# Revit family: 06-35-013-DN50-400
name_source: partatom
category: Pipe Accessories
units: mm (PartAtom-declared; Revit-internal decimal feet)

## family parameters
Always vertical = No
Cut with Voids When Loaded = No
Part Type = Valve - Breaks Into
Round Connector Dimension = Use Diameter
Shared = No
Work Plane-Based = No

## types (12) — shared parameters
Body_Wallthickness = 15 mm  [stored 0.0492126 ft]
DN 050 = Yes
DN050_PN10/16 = 06-050-35-01420
DN065_PN10/16 = 06-065-35-01420
DN080_PN10/16 = 06-080-35-01420
DN100_PN10/16 = 06-100-35-01420
DN125_PN10/16 = 06-125-35-01420
DN150_PN10/16 = 06-150-35-01420
DN200_PN10 = 06-200-35-00620
DN200_PN16 = 06-200-35-01620
DN250_PN10 = 06-250-35-00620
DN250_PN16 = 06-250-35-01620
DN300_PN10 = 06-300-35-00620
DN300_PN16 = 06-300-35-01620
DN350_PN10 = 06-350-35-00620
DN350_PN16 = 06-350-35-01620
DN400_PN10 = 06-400-35-00620
DN400_PN16 = 06-400-35-01620
Ftc = 4 mm  [stored 0.0131234 ft]
Name_Height_reference = 10 mm  [stored 0.0328084 ft]
Rib_Thickness = 18 mm  [stored 0.0590551 ft]
Search_table = 06-35-013-DN50-400
URL product pages = https://www.avkvalves.com
zero-valued in all types: Bottom_Reference

## per-type parameters (varying)
- DN 050: At=59 mm; Body_Height=100.5 mm; Body_depth=118 mm; Body_width=72 mm; Bonnet_Flange_Depth=118 mm; Bonnet_Flange_Width=82 mm; Bonnet_Flange_cut=7.5 mm  [stored 0.0246063 ft]; Bonnet_Flange_thickness=15 mm  [stored 0.0492126 ft]; Bonnet_Height=41.25 mm; Bonnet_Reference_height=90.5 mm; Bonnet_Thickness=73.44 mm; Bt=73.44 mm; Bt_2=66 mm; CL _Thickness=25 mm  [stored 0.082021 ft]; CL_Height=64 mm; Cut_Reference=300 mm; D=90 mm; D2=127 mm; DN 065=No; DN 080=No; DN 100=No; DN 125=No; DN 150=No; DN 200=No; DN 250=No; DN 300=No; DN 350=No; DN 400=No; Description_=AVK_GATE_VALVE,FLANGED; F1=16 mm  [stored 0.0524934 ft]; Fillet_Thickness=6 mm  [stored 0.019685 ft]; Flange_OR=82.5 mm; Flange_Thickness=19 mm  [stored 0.062336 ft]; Flange_Thickness_cut=28.75 mm; Ftc_reference_height=82.5 mm; H=329 mm; H1=202 mm; H3=412 mm; HW_Dia=15 mm  [stored 0.0492126 ft]; HW_H_ref=7.5 mm  [stored 0.0246063 ft]; HW_Rib_depth=167 mm; HW_Rib_width=15 mm  [stored 0.0492126 ft]; Horizontal_Flange_width=166 mm; ID (Radius)=25 mm  [stored 0.082021 ft]; L=150 mm; L_Dia=50 mm; Name_Reference=71 mm; Name_Width=36 mm  [stored 0.11811 ft]; Neck_H=37.5 mm; Neck_T=23 mm  [stored 0.0754593 ft]; Neck_T2=21 mm; Nominal Diameter (DN)=50 mm; R1tv=825 mm; R2f=15 mm  [stored 0.0492126 ft]; RF_Dia=49 mm; Rf=276.67 mm; Rib_Height_Reference_1=120 mm; Rib_Height_Reference_2=110 mm; Rib_Height_Reference_3=100 mm; Rib_Height_Reference_4=60 mm; Rib_Width_1=36 mm  [stored 0.11811 ft]; Rib_Width_2=36 mm  [stored 0.11811 ft]; Rib_Width_3=36 mm  [stored 0.11811 ft]; Rib_depth_1=36 mm  [stored 0.11811 ft]; Rib_depth_2=36 mm  [stored 0.11811 ft]; Rib_depth_3=36 mm  [stored 0.11811 ft]; Rt=275 mm
- DN 065: At=53.5 mm; Body_Height=115 mm; Body_depth=107 mm; Body_width=60 mm; Bonnet_Flange_Depth=135 mm; Bonnet_Flange_Width=65 mm; Bonnet_Flange_cut=7.5 mm  [stored 0.0246063 ft]; Bonnet_Flange_thickness=15 mm  [stored 0.0492126 ft]; Bonnet_Height=46.5 mm; Bonnet_Reference_height=105 mm; Bonnet_Thickness=61.2 mm; Bt=61.2 mm; Bt_2=54 mm; CL _Thickness=19 mm  [stored 0.062336 ft]; CL_Height=58.5 mm; Cut_Reference=340 mm; D=112.5 mm; D2=128 mm; DN 065=Yes; DN 080=Yes; DN 100=Yes; DN 125=Yes; DN 150=Yes; DN 200=Yes; DN 250=Yes; DN 300=Yes; DN 350=Yes; DN 400=Yes; Description_=AVK_GATE-VALVE,FLANGED; F1=20 mm  [stored 0.0656168 ft]; Fillet_Thickness=6 mm  [stored 0.019685 ft]; Flange_OR=93 mm; Flange_Thickness=19 mm  [stored 0.062336 ft]; Flange_Thickness_cut=30.25 mm  [stored 0.0992454 ft]; Ftc_reference_height=93 mm; H=355 mm; H1=227 mm; H3=448 mm; HW_Dia=15 mm  [stored 0.0492126 ft]; HW_H_ref=7.5 mm  [stored 0.0246063 ft]; HW_Rib_depth=212 mm; HW_Rib_width=15 mm  [stored 0.0492126 ft]; Horizontal_Flange_width=186 mm; ID (Radius)=32.5 mm  [stored 0.106627 ft]; L=170 mm; L_Dia=65 mm; Name_Reference=96 mm; Name_Width=30 mm  [stored 0.0984252 ft]; Neck_H=53.5 mm; Neck_T=17 mm  [stored 0.0557743 ft]; Neck_T2=15 mm  [stored 0.0492126 ft]; Nominal Diameter (DN)=65 mm; R1tv=930 mm; R2f=15 mm  [stored 0.0492126 ft]; RF_Dia=59 mm; Rf=310 mm; Rib_Height_Reference_1=120 mm; Rib_Height_Reference_2=110 mm; Rib_Height_Reference_3=100 mm; Rib_Height_Reference_4=75 mm; Rib_Width_1=30 mm  [stored 0.0984252 ft]; Rib_Width_2=30 mm  [stored 0.0984252 ft]; Rib_Width_3=30 mm  [stored 0.0984252 ft]; Rib_depth_1=30 mm  [stored 0.0984252 ft]; Rib_depth_2=30 mm  [stored 0.0984252 ft]; Rib_depth_3=30 mm  [stored 0.0984252 ft]; Rt=310 mm
- DN 080: At=81.3 mm; Body_Height=136 mm; Body_depth=162.6 mm; Body_width=75 mm; Bonnet_Flange_Depth=160 mm; Bonnet_Flange_Width=96 mm; Bonnet_Flange_cut=7.5 mm  [stored 0.0246063 ft]; Bonnet_Flange_thickness=15 mm  [stored 0.0492126 ft]; Bonnet_Height=50 mm; Bonnet_Reference_height=126 mm; Bonnet_Thickness=76.5 mm; Bt=76.5 mm; Bt_2=69 mm; CL _Thickness=26.5 mm  [stored 0.0869423 ft]; CL_Height=86.3 mm; Cut_Reference=360 mm; D=112.5 mm; D2=135 mm; DN 065=Yes; DN 080=Yes; DN 100=Yes; DN 125=Yes; DN 150=Yes; DN 200=Yes; DN 250=Yes; DN 300=Yes; DN 350=Yes; DN 400=Yes; Description_=AVK_GATE_VALVE,FLANGED; F1=20 mm  [stored 0.0656168 ft]; Fillet_Thickness=6 mm  [stored 0.019685 ft]; Flange_OR=100 mm; Flange_Thickness=19 mm  [stored 0.062336 ft]; Flange_Thickness_cut=30 mm  [stored 0.0984252 ft]; Ftc_reference_height=100 mm; H=382 mm; H1=247 mm; H3=482 mm; HW_Dia=15 mm  [stored 0.0492126 ft]; HW_H_ref=7.5 mm  [stored 0.0246063 ft]; HW_Rib_depth=212 mm; HW_Rib_width=15 mm  [stored 0.0492126 ft]; Horizontal_Flange_width=200 mm; ID (Radius)=40 mm; L=180 mm; L_Dia=80 mm; Name_Reference=90 mm; Name_Width=37.5 mm; Neck_H=24.7 mm; Neck_T=24.5 mm  [stored 0.0803806 ft]; Neck_T2=22.5 mm; Nominal Diameter (DN)=80 mm; R1tv=1000 mm; R2f=15 mm  [stored 0.0492126 ft]; RF_Dia=66.9 mm; Rf=333.33 mm; Rib_Height_Reference_1=120 mm; Rib_Height_Reference_2=110 mm; Rib_Height_Reference_3=100 mm; Rib_Height_Reference_4=85 mm; Rib_Width_1=37.5 mm; Rib_Width_2=37.5 mm; Rib_Width_3=37.5 mm; Rib_depth_1=37.5 mm; Rib_depth_2=37.5 mm; Rib_depth_3=37.5 mm; Rt=333.33 mm
- DN 100: At=76.5 mm; Body_Height=148 mm; Body_depth=153 mm; Body_width=80 mm; Bonnet_Flange_Depth=180 mm; Bonnet_Flange_Width=81 mm; Bonnet_Flange_cut=7.5 mm  [stored 0.0246063 ft]; Bonnet_Flange_thickness=15 mm  [stored 0.0492126 ft]; Bonnet_Height=55 mm; Bonnet_Reference_height=138 mm; Bonnet_Thickness=81.6 mm; Bt=81.6 mm; Bt_2=74 mm; CL _Thickness=29 mm  [stored 0.0951444 ft]; CL_Height=81.5 mm; Cut_Reference=380 mm; D=140 mm; D2=144 mm; DN 065=Yes; DN 080=Yes; DN 100=Yes; DN 125=Yes; DN 150=Yes; DN 200=Yes; DN 250=Yes; DN 300=Yes; DN 350=Yes; DN 400=Yes; Description_=AVK_GATE_VALVE,FLANGED; F1=22 mm  [stored 0.0721785 ft]; Fillet_Thickness=6 mm  [stored 0.019685 ft]; Flange_OR=110 mm; Flange_Thickness=19 mm  [stored 0.062336 ft]; Flange_Thickness_cut=30 mm  [stored 0.0984252 ft]; Ftc_reference_height=110 mm; H=414 mm; H1=270 mm; H3=524 mm; HW_Dia=15 mm  [stored 0.0492126 ft]; HW_H_ref=7.5 mm  [stored 0.0246063 ft]; HW_Rib_depth=267 mm; HW_Rib_width=15 mm  [stored 0.0492126 ft]; Horizontal_Flange_width=220 mm; ID (Radius)=50 mm; L=190 mm; L_Dia=100 mm; Name_Reference=101 mm; Name_Width=40 mm; Neck_H=40.5 mm; Neck_T=27 mm  [stored 0.0885827 ft]; Neck_T2=25 mm  [stored 0.082021 ft]; Nominal Diameter (DN)=100 mm; R1tv=1100 mm; R2f=15 mm  [stored 0.0492126 ft]; RF_Dia=76.5 mm; Rf=366.67 mm; Rib_Height_Reference_1=120 mm; Rib_Height_Reference_2=110 mm; Rib_Height_Reference_3=100 mm; Rib_Height_Reference_4=90 mm; Rib_Width_1=40 mm; Rib_Width_2=40 mm; Rib_Width_3=40 mm; Rib_depth_1=40 mm; Rib_depth_2=40 mm; Rib_depth_3=40 mm; Rt=366.67 mm
- DN 150: At=109 mm; Body_Height=205 mm; Body_depth=218 mm; Body_width=95 mm; Bonnet_Flange_Depth=250 mm; Bonnet_Flange_Width=116 mm; Bonnet_Flange_cut=7.5 mm  [stored 0.0246063 ft]; Bonnet_Flange_thickness=15 mm  [stored 0.0492126 ft]; Bonnet_Height=71.25 mm; Bonnet_Reference_height=195 mm; Bonnet_Thickness=96.9 mm; Bt=96.9 mm; Bt_2=89 mm; CL _Thickness=33.5 mm; CL_Height=114 mm; Cut_Reference=420 mm; D=160 mm; D2=175 mm; DN 065=Yes; DN 080=Yes; DN 100=Yes; DN 125=Yes; DN 150=Yes; DN 200=Yes; DN 250=Yes; DN 300=Yes; DN 350=Yes; DN 400=Yes; Description_=AVK_GATE_VALVE,FLANGED; F1=22 mm  [stored 0.0721785 ft]; Fillet_Thickness=12 mm  [stored 0.0393701 ft]; Flange_OR=142.5 mm; Flange_Thickness=19 mm  [stored 0.062336 ft]; Flange_Thickness_cut=33.75 mm  [stored 0.110728 ft]; Ftc_reference_height=142.5 mm; H=540 mm; H1=365 mm; H3=683 mm; HW_Dia=15 mm  [stored 0.0492126 ft]; HW_H_ref=7.5 mm  [stored 0.0246063 ft]; HW_Rib_depth=307 mm; HW_Rib_width=15 mm  [stored 0.0492126 ft]; Horizontal_Flange_width=286 mm; ID (Radius)=75 mm; L=210 mm; L_Dia=150 mm; Name_Reference=143 mm; Name_Width=47.5 mm; Neck_H=46 mm; Neck_T=31.5 mm  [stored 0.103346 ft]; Neck_T2=29.5 mm; Nominal Diameter (DN)=150 mm; R1tv=1425 mm; R2f=30 mm  [stored 0.0984252 ft]; RF_Dia=104.5 mm; Rf=476.67 mm; Rib_Height_Reference_1=120 mm; Rib_Height_Reference_2=110 mm; Rib_Height_Reference_3=100 mm; Rib_Height_Reference_4=150 mm; Rib_Width_1=47.5 mm; Rib_Width_2=47.5 mm; Rib_Width_3=47.5 mm; Rib_depth_1=47.5 mm; Rib_depth_2=47.5 mm; Rib_depth_3=47.5 mm; Rt=475 mm
- DN 200: At=126 mm; Body_Height=289 mm; Body_depth=252 mm; Body_width=108 mm; Bonnet_Flange_Depth=283 mm; Bonnet_Flange_Width=186 mm; Bonnet_Flange_cut=12.5 mm  [stored 0.0410105 ft]; Bonnet_Flange_thickness=25 mm  [stored 0.082021 ft]; Bonnet_Height=85 mm; Bonnet_Reference_height=279 mm; Bonnet_Thickness=110.16 mm; Bt=110.16 mm; Bt_2=102 mm; CL _Thickness=34 mm  [stored 0.111549 ft]; CL_Height=131 mm; Cut_Reference=460 mm; D=180 mm; D2=232 mm; DN 065=Yes; DN 080=Yes; DN 100=Yes; DN 125=Yes; DN 150=Yes; DN 200=Yes; DN 250=Yes; DN 300=Yes; DN 350=Yes; DN 400=Yes; Description_=AVK_GATE_VALVE,FLANGED; F1=28 mm  [stored 0.0918635 ft]; Fillet_Thickness=24 mm  [stored 0.0787402 ft]; Flange_OR=170 mm; Flange_Thickness=20 mm  [stored 0.0656168 ft]; Flange_Thickness_cut=35 mm  [stored 0.114829 ft]; Ftc_reference_height=170 mm; H=688 mm; H1=456 mm; H3=858 mm; HW_Dia=20 mm  [stored 0.0656168 ft]; HW_H_ref=10 mm  [stored 0.0328084 ft]; HW_Rib_depth=342 mm; HW_Rib_width=20 mm  [stored 0.0656168 ft]; Horizontal_Flange_width=340 mm; ID (Radius)=100 mm; L=230 mm; L_Dia=200 mm; Name_Reference=183 mm; Name_Width=54 mm; Neck_H=36 mm  [stored 0.11811 ft]; Neck_T=32 mm  [stored 0.104987 ft]; Neck_T2=30 mm  [stored 0.0984252 ft]; Nominal Diameter (DN)=200 mm; R1tv=1700 mm; R2f=60 mm; RF_Dia=132 mm; Rf=566.67 mm; Rib_Height_Reference_1=120 mm; Rib_Height_Reference_2=110 mm; Rib_Height_Reference_3=100 mm; Rib_Height_Reference_4=180 mm; Rib_Width_1=54 mm; Rib_Width_2=54 mm; Rib_Width_3=54 mm; Rib_depth_1=54 mm; Rib_depth_2=54 mm; Rib_depth_3=54 mm; Rt=566.67 mm
- DN 250: At=171 mm; Body_Height=305 mm; Body_depth=342 mm; Body_width=124 mm; Bonnet_Flange_Depth=372 mm; Bonnet_Flange_Width=158 mm; Bonnet_Flange_cut=12.5 mm  [stored 0.0410105 ft]; Bonnet_Flange_thickness=25 mm  [stored 0.082021 ft]; Bonnet_Height=100 mm; Bonnet_Reference_height=295 mm; Bonnet_Thickness=126.48 mm; Bt=126.48 mm; Bt_2=118 mm; CL _Thickness=42 mm; CL_Height=176 mm; Cut_Reference=500 mm; D=250 mm; D2=225 mm; DN 065=Yes; DN 080=Yes; DN 100=Yes; DN 125=Yes; DN 150=Yes; DN 200=Yes; DN 250=Yes; DN 300=Yes; DN 350=Yes; DN 400=Yes; Description_=AVK_GATE_VALVE,FLANGED; F1=27 mm  [stored 0.0885827 ft]; Fillet_Thickness=24 mm  [stored 0.0787402 ft]; Flange_OR=200 mm; Flange_Thickness=22 mm  [stored 0.0721785 ft]; Flange_Thickness_cut=37.5 mm; Ftc_reference_height=200 mm; H=780 mm; H1=555 mm; H3=980 mm; HW_Dia=20 mm  [stored 0.0656168 ft]; HW_H_ref=10 mm  [stored 0.0328084 ft]; HW_Rib_depth=482 mm; HW_Rib_width=20 mm  [stored 0.0656168 ft]; Horizontal_Flange_width=400 mm; ID (Radius)=125 mm; L=250 mm; L_Dia=250 mm; Name_Reference=270 mm; Name_Width=62 mm; Neck_H=74 mm; Neck_T=40 mm; Neck_T2=38 mm; Nominal Diameter (DN)=250 mm; R1tv=2000 mm; R2f=60 mm; RF_Dia=159.5 mm; Rf=666.67 mm; Rib_Height_Reference_1=90 mm; Rib_Height_Reference_2=110 mm; Rib_Height_Reference_3=100 mm; Rib_Height_Reference_4=200 mm; Rib_Width_1=140 mm; Rib_Width_2=140 mm; Rib_Width_3=62 mm; Rib_depth_1=400 mm; Rib_depth_2=62 mm; Rib_depth_3=62 mm; Rt=666.67 mm
- DN 300: At=208.5 mm; Body_Height=370 mm; Body_depth=417 mm; Body_width=157 mm; Bonnet_Flange_Depth=448 mm; Bonnet_Flange_Width=206 mm; Bonnet_Flange_cut=17.5 mm  [stored 0.0574147 ft]; Bonnet_Flange_thickness=35 mm  [stored 0.114829 ft]; Bonnet_Height=113.75 mm; Bonnet_Reference_height=360 mm; Bonnet_Thickness=160.14 mm; Bt=160.14 mm; Bt_2=151 mm; CL _Thickness=58.5 mm; CL_Height=213.5 mm; Cut_Reference=540 mm; D=250 mm; D2=225 mm; DN 065=Yes; DN 080=Yes; DN 100=Yes; DN 125=Yes; DN 150=Yes; DN 200=Yes; DN 250=Yes; DN 300=Yes; DN 350=Yes; DN 400=Yes; Description_=AVK_GATE_VALVE,FLANGED; F1=27 mm  [stored 0.0885827 ft]; Fillet_Thickness=24 mm  [stored 0.0787402 ft]; Flange_OR=227.5 mm; Flange_Thickness=24.5 mm  [stored 0.0803806 ft]; Flange_Thickness_cut=38.75 mm; Ftc_reference_height=227.5 mm; H=855 mm; H1=630 mm; H3=1083 mm; HW_Dia=25 mm  [stored 0.082021 ft]; HW_H_ref=12.5 mm  [stored 0.0410105 ft]; HW_Rib_depth=477 mm; HW_Rib_width=25 mm  [stored 0.082021 ft]; Horizontal_Flange_width=456 mm; ID (Radius)=150 mm; L=270 mm; L_Dia=300 mm; Name_Reference=250 mm; Name_Width=78.5 mm; Neck_H=46.5 mm; Neck_T=56.5 mm; Neck_T2=54.5 mm; Nominal Diameter (DN)=300 mm; R1tv=2275 mm; R2f=60 mm; RF_Dia=183.5 mm; Rf=760 mm; Rib_Height_Reference_1=178 mm; Rib_Height_Reference_2=285 mm; Rib_Height_Reference_3=150 mm; Rib_Height_Reference_4=300 mm; Rib_Width_1=168 mm; Rib_Width_2=168 mm; Rib_Width_3=78.5 mm; Rib_depth_1=465 mm; Rib_depth_2=465 mm; Rib_depth_3=78.5 mm; Rt=758.33 mm
- DN 350: At=250 mm; Body_Height=485 mm; Body_depth=500 mm; Body_width=170 mm; Bonnet_Flange_Depth=554 mm; Bonnet_Flange_Width=180 mm; Bonnet_Flange_cut=17.5 mm  [stored 0.0574147 ft]; Bonnet_Flange_thickness=35 mm  [stored 0.114829 ft]; Bonnet_Height=130 mm; Bonnet_Reference_height=475 mm; Bonnet_Thickness=173.4 mm; Bt=173.4 mm; Bt_2=164 mm; CL _Thickness=65 mm; CL_Height=255 mm; Cut_Reference=580 mm; D=320 mm; D2=130 mm; DN 065=Yes; DN 080=Yes; DN 100=Yes; DN 125=Yes; DN 150=Yes; DN 200=Yes; DN 250=Yes; DN 300=Yes; DN 350=Yes; DN 400=Yes; Description_=AVK_GATE_VALVE,FLANGED; F1=37 mm  [stored 0.121391 ft]; Fillet_Thickness=24 mm  [stored 0.0787402 ft]; Flange_OR=260 mm; Flange_Thickness=26.5 mm  [stored 0.0869423 ft]; Flange_Thickness_cut=42.5 mm; Ftc_reference_height=260 mm; H=930 mm; H1=800 mm; H3=1190 mm; HW_Dia=25 mm  [stored 0.082021 ft]; HW_H_ref=12.5 mm  [stored 0.0410105 ft]; HW_Rib_depth=617 mm; HW_Rib_width=25 mm  [stored 0.082021 ft]; Horizontal_Flange_width=520 mm; ID (Radius)=175 mm; L=290 mm; L_Dia=350 mm; Name_Reference=404 mm; Name_Width=85 mm; Neck_H=60 mm; Neck_T=63 mm; Neck_T2=61 mm; Nominal Diameter (DN)=350 mm; R1tv=2600 mm; R2f=60 mm; RF_Dia=215 mm; Rf=866.67 mm; Rib_Height_Reference_1=70 mm; Rib_Height_Reference_2=185 mm; Rib_Height_Reference_3=305 mm; Rib_Height_Reference_4=410 mm; Rib_Width_1=190 mm; Rib_Width_2=190 mm; Rib_Width_3=190 mm; Rib_depth_1=560 mm; Rib_depth_2=560 mm; Rib_depth_3=560 mm; Rt=866.67 mm
- DN 400-PN/10: At=238 mm; Body_Height=512 mm; Body_depth=476 mm; Body_width=172 mm; Bonnet_Flange_Depth=554 mm; Bonnet_Flange_Width=250 mm; Bonnet_Flange_cut=35 mm  [stored 0.114829 ft]; Bonnet_Flange_thickness=70 mm; Bonnet_Height=145 mm; Bonnet_Reference_height=502 mm; Bonnet_Thickness=175.44 mm; Bt=175.44 mm; Bt_2=166 mm; CL _Thickness=62 mm; CL_Height=243 mm; Cut_Reference=620 mm; D=320 mm; D2=204 mm; DN 065=Yes; DN 080=Yes; DN 100=Yes; DN 125=Yes; DN 150=Yes; DN 200=Yes; DN 250=Yes; DN 300=Yes; DN 350=Yes; DN 400=Yes; Description_=AVK_GATE_VALVE,FLANGED; F1=37 mm  [stored 0.121391 ft]; Fillet_Thickness=32 mm  [stored 0.104987 ft]; Flange_OR=290 mm; Flange_Thickness=28 mm  [stored 0.0918635 ft]; Flange_Thickness_cut=44.98 mm; Ftc_reference_height=290 mm; H=1064 mm; H1=860 mm; H3=1354 mm; HW_Dia=30 mm  [stored 0.0984252 ft]; HW_H_ref=15 mm  [stored 0.0492126 ft]; HW_Rib_depth=612 mm; HW_Rib_width=30 mm  [stored 0.0984252 ft]; Horizontal_Flange_width=580 mm; ID (Radius)=200.05 mm; L=310 mm; L_Dia=400.1 mm; Name_Reference=426 mm; Name_Width=86 mm; Neck_H=105 mm; Neck_T=60 mm; Neck_T2=58 mm; Nominal Diameter (DN)=400.1 mm; R1tv=2900 mm; R2f=80 mm; RF_Dia=241 mm; Rf=966.67 mm; Rib_Height_Reference_1=81 mm; Rib_Height_Reference_2=210 mm; Rib_Height_Reference_3=330 mm; Rib_Height_Reference_4=440 mm; Rib_Width_1=248 mm; Rib_Width_2=248 mm; Rib_Width_3=248 mm; Rib_depth_1=564 mm; Rib_depth_2=564 mm; Rib_depth_3=564 mm; Rt=966.67 mm
- DN 125: At=92.5 mm; Body_Height=170 mm; Body_depth=185 mm; Body_width=90 mm; Bonnet_Flange_Depth=235 mm; Bonnet_Flange_Width=83 mm; Bonnet_Flange_cut=7.5 mm  [stored 0.0246063 ft]; Bonnet_Flange_thickness=15 mm  [stored 0.0492126 ft]; Bonnet_Height=62.5 mm; Bonnet_Reference_height=160 mm; Bonnet_Thickness=91.8 mm; Bt=91.8 mm; Bt_2=84 mm; CL _Thickness=34 mm  [stored 0.111549 ft]; CL_Height=97.5 mm; Cut_Reference=400 mm; D=160 mm; D2=150 mm; DN 065=Yes; DN 080=Yes; DN 100=Yes; DN 125=Yes; DN 150=Yes; DN 200=Yes; DN 250=Yes; DN 300=Yes; DN 350=Yes; DN 400=Yes; Description_=AVK_GATE_VALVE,FLANGED; F1=22 mm  [stored 0.0721785 ft]; Fillet_Thickness=6 mm  [stored 0.019685 ft]; Flange_OR=125 mm; Flange_Thickness=19 mm  [stored 0.062336 ft]; Flange_Thickness_cut=31.25 mm  [stored 0.102526 ft]; Ftc_reference_height=125 mm; H=461 mm; H1=311 mm; H3=586 mm; HW_Dia=15 mm  [stored 0.0492126 ft]; HW_H_ref=7.5 mm  [stored 0.0246063 ft]; HW_Rib_depth=307 mm; HW_Rib_width=15 mm  [stored 0.0492126 ft]; Horizontal_Flange_width=250 mm; ID (Radius)=62.5 mm; L=200 mm; L_Dia=125 mm; Name_Reference=114 mm; Name_Width=45 mm; Neck_H=43.5 mm; Neck_T=32 mm  [stored 0.104987 ft]; Neck_T2=30 mm  [stored 0.0984252 ft]; Nominal Diameter (DN)=125 mm; R1tv=1250 mm; R2f=15 mm  [stored 0.0492126 ft]; RF_Dia=91.5 mm; Rf=416.67 mm; Rib_Height_Reference_1=120 mm; Rib_Height_Reference_2=110 mm; Rib_Height_Reference_3=100 mm; Rib_Height_Reference_4=120 mm; Rib_Width_1=45 mm; Rib_Width_2=45 mm; Rib_Width_3=45 mm; Rib_depth_1=45 mm; Rib_depth_2=45 mm; Rib_depth_3=45 mm; Rt=416.67 mm
- DN 400-PN/16: At=238 mm; Body_Height=512 mm; Body_depth=476 mm; Body_width=172 mm; Bonnet_Flange_Depth=554 mm; Bonnet_Flange_Width=250 mm; Bonnet_Flange_cut=35 mm  [stored 0.114829 ft]; Bonnet_Flange_thickness=70 mm; Bonnet_Height=145 mm; Bonnet_Reference_height=502 mm; Bonnet_Thickness=175.44 mm; Bt=175.44 mm; Bt_2=166 mm; CL _Thickness=62 mm; CL_Height=243 mm; Cut_Reference=620 mm; D=320 mm; D2=204 mm; DN 065=Yes; DN 080=Yes; DN 100=Yes; DN 125=Yes; DN 150=Yes; DN 200=Yes; DN 250=Yes; DN 300=Yes; DN 350=Yes; DN 400=Yes; Description_=AVK_GATE_VALVE,FLANGED; F1=37 mm  [stored 0.121391 ft]; Fillet_Thickness=32 mm  [stored 0.104987 ft]; Flange_OR=290 mm; Flange_Thickness=28 mm  [stored 0.0918635 ft]; Flange_Thickness_cut=44.96 mm; Ftc_reference_height=290 mm; H=1064 mm; H1=860 mm; H3=1354 mm; HW_Dia=30 mm  [stored 0.0984252 ft]; HW_H_ref=15 mm  [stored 0.0492126 ft]; HW_Rib_depth=612 mm; HW_Rib_width=30 mm  [stored 0.0984252 ft]; Horizontal_Flange_width=580 mm; ID (Radius)=200.08 mm; L=310 mm; L_Dia=400.16 mm; Name_Reference=426 mm; Name_Width=86 mm; Neck_H=105 mm; Neck_T=60 mm; Neck_T2=58 mm; Nominal Diameter (DN)=400.16 mm; R1tv=2900 mm; R2f=80 mm; RF_Dia=241 mm; Rf=966.67 mm; Rib_Height_Reference_1=81 mm; Rib_Height_Reference_2=210 mm; Rib_Height_Reference_3=330 mm; Rib_Height_Reference_4=440 mm; Rib_Width_1=248 mm; Rib_Width_2=248 mm; Rib_Width_3=248 mm; Rib_depth_1=564 mm; Rib_depth_2=564 mm; Rib_depth_3=564 mm; Rt=966.67 mm

note: [stored X ft] marks values corroborated as IEEE doubles in the binary element streams (Revit-internal decimal feet)

## geometry (parser evidence)
native form markers: Sweep x5
no freeform markers — native parametric forms only
